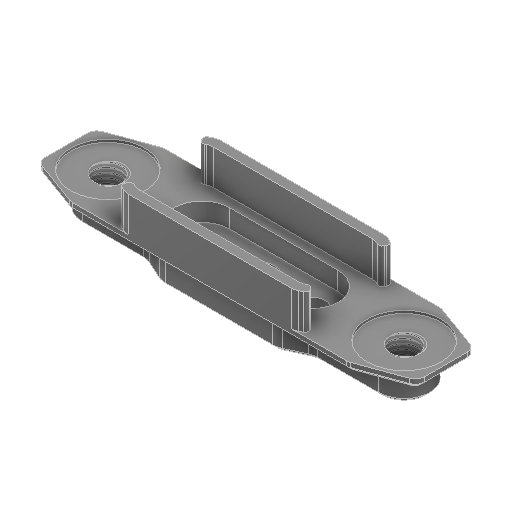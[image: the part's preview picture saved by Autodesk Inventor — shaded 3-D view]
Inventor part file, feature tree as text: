
AUTODESK INVENTOR PART (.ipt)
format: ipt  version: 2022 (Build 260153000, 153)  size: 465,408 bytes
history: mixed  units: in
note: dims shown in document units (in); Inventor stores cm internally (conversion verified against a paired STEP export)
features: thread x1, imported_body x1
ambient origin geometry x8: Origin, YZ Plane, XZ Plane, XY Plane, X Axis, Y Axis, Z Axis, Center Point
bodies: Solid1 (imported_parasolid)
feature tree (2):
  thread  "Thread5"  [1 undecoded]
  imported_body  NMx_Import_Brep_tag  [imported B-rep: ~6 faces, bbox_mm=None]
note: 1 required parameter value undecoded (feature->parameter linkage not recoverable at this tier; creation-order binding heuristic only, values carry confidence <= 0.55)
